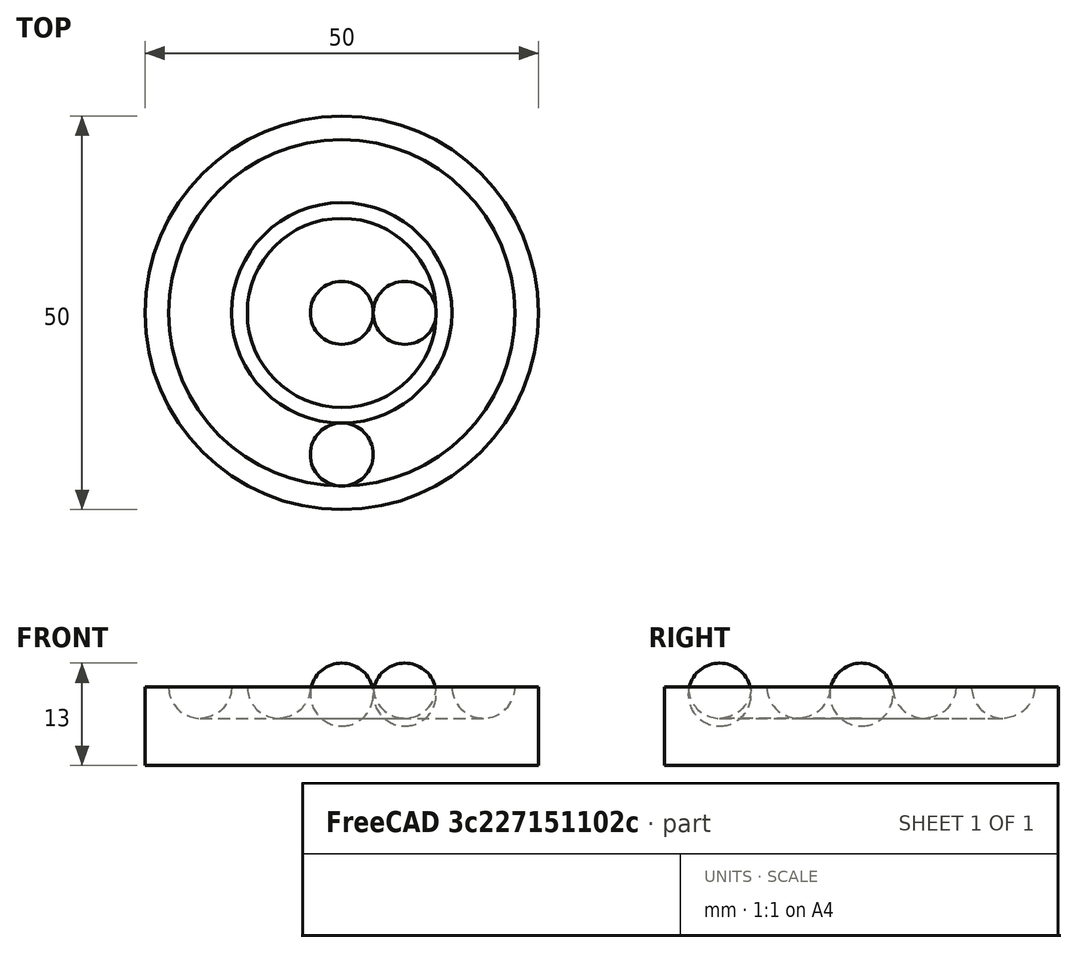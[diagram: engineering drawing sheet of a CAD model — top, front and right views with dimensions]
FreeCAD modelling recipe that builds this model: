
FCSTD DOCUMENT  (FreeCAD 0.21R33694 (Git))
Label: OJT1_T15R02_espiral
License: All rights reserved
LicenseURL: http://en.wikipedia.org/wiki/All_rights_reserved
objects: Part::Torus×2, Part::Cut×2, Part::Sphere×2, Part::Cylinder×1
note: 7 computed .brp shape members not serialized (recipe doc carries the construction recipe); baked Part::Feature solids carry a one-line shape summary decoded from their .brp

FEATURE [Part::Cylinder] Cylinder
  Angle = 360
  AttacherType = Attacher::AttachEngine3D
  FirstAngle = 0
  Height = 10
  Radius = 25
  SecondAngle = 0
FEATURE [Part::Torus] Torus  label="part_1"
  Angle1 = -180
  Angle2 = 180
  Angle3 = 360
  AttacherType = Attacher::AttachEngine3D
  Placement = pos=(0,0,10) rot=(0,0,1;0rad)
  Radius1 = 8
  Radius2 = 4
FEATURE [Part::Torus] Torus001  label="part_002"
  Angle1 = -180
  Angle2 = 180
  Angle3 = 360
  AttacherType = Attacher::AttachEngine3D
  Placement = pos=(0,0,10) rot=(0,0,1;0rad)
  Radius1 = 18
  Radius2 = 4
FEATURE [Part::Cut] Cut
  Base = -> Cylinder
  Refine = true
  Tool = -> Torus
FEATURE [Part::Cut] Cut001
  Base = -> Cut
  Refine = true
  Tool = -> Torus001
FEATURE [Part::Sphere] Sphere
  Angle1 = -90
  Angle2 = 90
  Angle3 = 360
  AttacherType = Attacher::AttachEngine3D
  Placement = pos=(8,0,9) rot=(0,0,1;0rad)
  Radius = 4
FEATURE [Part::Sphere] Sphere001
  Angle1 = -90
  Angle2 = 90
  Angle3 = 360
  AttacherType = Attacher::AttachEngine3D
  Placement = pos=(0,-18,9) rot=(0,0,1;0rad)
  Radius = 4
